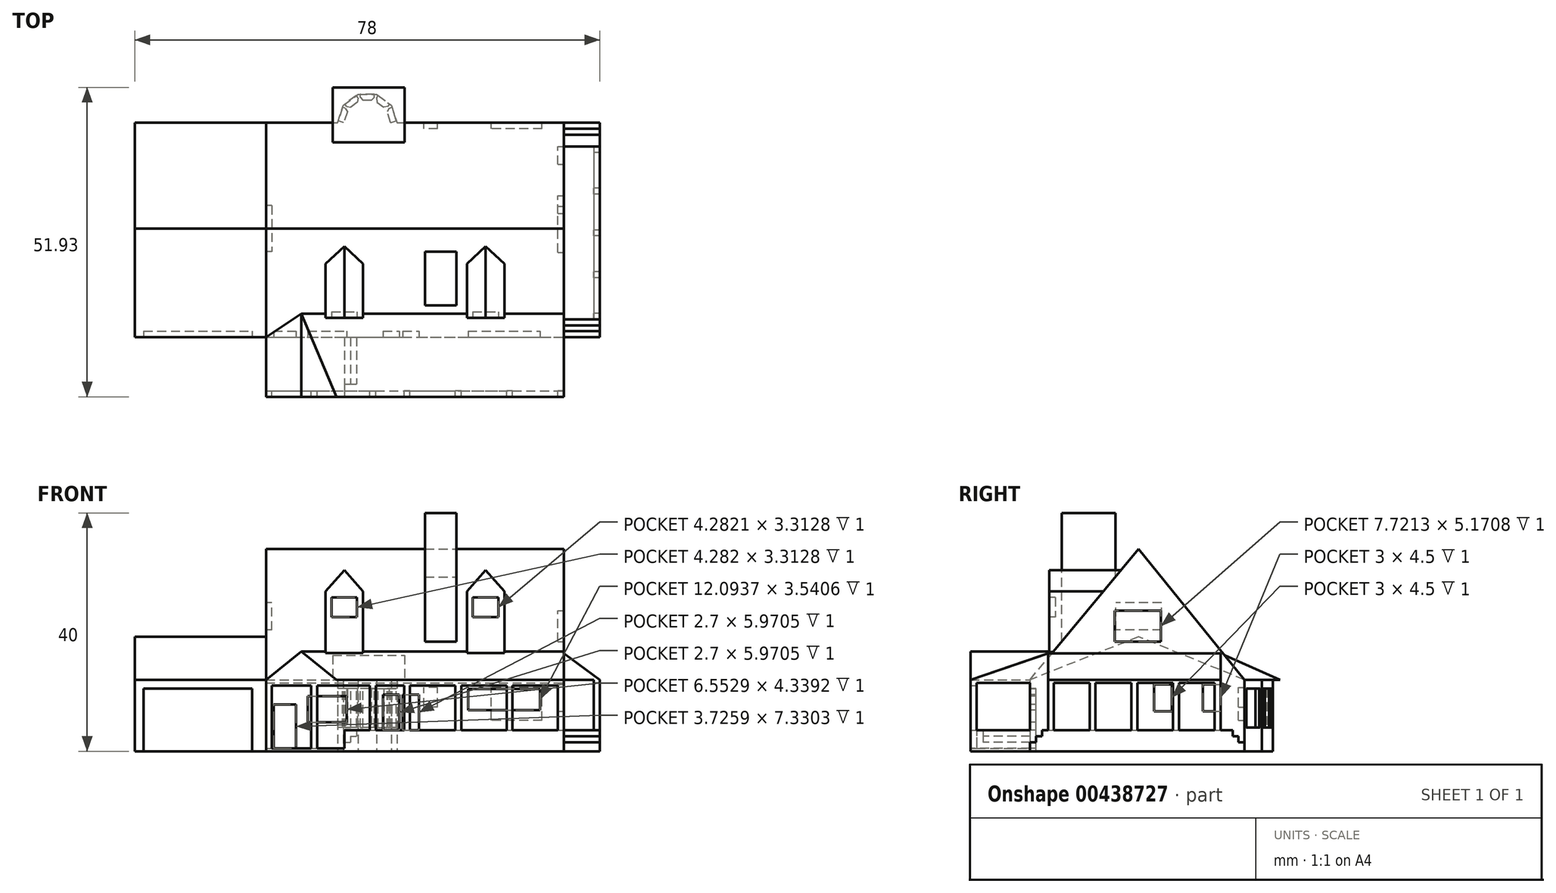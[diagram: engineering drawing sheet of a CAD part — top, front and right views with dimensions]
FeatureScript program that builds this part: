
annotation { "Feature Type Name" : "Feature", "Feature Type Description" : "" }
export const myFeature = defineFeature(function(context is Context, id is Id, definition is map)
    precondition{}
    {
        {
            var Q0;
            Q0=qCreatedBy(makeId("Top.planeOp"),FACE);
            var sketch = newSketch(context, id + "F0", { "sketchPlane" : qUnion([Q0])});
            skLineSegment(sketch, "E0.bottom", {"start": v(-54, 17.76) * mm, "end": v(18, 17.76) * mm});
            skLineSegment(sketch, "E0.top", {"start": v(-54, -18.24) * mm, "end": v(18, -18.24) * mm});
            skLineSegment(sketch, "E0.left", {"start": v(-54, 17.76) * mm, "end": v(-54, -18.24) * mm});
            skLineSegment(sketch, "E0.right", {"start": v(18, 17.76) * mm, "end": v(18, -18.24) * mm});
            skSolve(sketch);
        }
        {
            var Q0;
            Q0=makeQuery(id+"F0.imprint","IMPRINT",FACE,{"disambiguationData":[TD([[makeQuery(id+"F0.imprint","IMPRINT",EDGE,{"derivedFrom":sQuery(id+"F0.wireOp",EDGE,"E0.bottom")}),-1.0]])]});
            extrude(context, id + "F1", {"entities" : qUnion([Q0]), "depth" : 12 * mm});
        }
        {
            var Q0;
            Q0=makeQuery(id+"F1.opExtrude","SWEPT_FACE",FACE,{"disambiguationData":[OSD([sQuery(id+"F0.wireOp",EDGE,"E0.right")])]});
            var sketch = newSketch(context, id + "F2", { "sketchPlane" : qUnion([Q0])});
            skLineSegment(sketch, "E1.0", {"start": v(17.76, 12) * mm, "end": v(-18.24, 12) * mm});
            skLineSegment(sketch, "E2", {"start": v(-18.24, 12) * mm, "end": v(0, 33.97) * mm});
            skLineSegment(sketch, "E3", {"start": v(0, 33.97) * mm, "end": v(17.76, 12) * mm});
            skSolve(sketch);
        }
        {
            var Q0;
            Q0=makeQuery(id+"F2.imprint","IMPRINT",FACE,{"disambiguationData":[TD([[makeQuery(id+"F2.imprint","IMPRINT",EDGE,{"derivedFrom":sQuery(id+"F2.wireOp",EDGE,"E1.0")}),-1.0]])]});
            extrude(context, id + "F3", {"entities" : qUnion([Q0]), "operationType" : NewBodyOperationType.ADD, "oppositeDirection" : true, "depth" : 50 * mm});
        }
        {
            var Q0;
            Q0=makeQuery(id+"F1.opExtrude","SWEPT_FACE",FACE,{"disambiguationData":[OSD([sQuery(id+"F0.wireOp",EDGE,"E0.left")])]});
            var sketch = newSketch(context, id + "F4", { "sketchPlane" : qUnion([Q0])});
            skLineSegment(sketch, "E4.0", {"start": v(-17.76, 12) * mm, "end": v(18.24, 12) * mm});
            skLineSegment(sketch, "E5", {"start": v(-17.76, 12) * mm, "end": v(0, 19.2) * mm});
            skLineSegment(sketch, "E6", {"start": v(0, 19.2) * mm, "end": v(18.24, 12) * mm});
            skSolve(sketch);
        }
        {
            var Q0;
            Q0=makeQuery(id+"F4.imprint","IMPRINT",FACE,{"disambiguationData":[TD([[makeQuery(id+"F4.imprint","IMPRINT",EDGE,{"derivedFrom":sQuery(id+"F4.wireOp",EDGE,"E4.0")}),1.0]])]});
            extrude(context, id + "F5", {"entities" : qUnion([Q0]), "operationType" : NewBodyOperationType.ADD, "endBound" : BoundingType.UP_TO_NEXT, "oppositeDirection" : true, "depth" : 25 * mm});
        }
        {
            var Q0;
            Q0=makeQuery(id+"F1.opExtrude","SWEPT_FACE",FACE,{"disambiguationData":[OSD([sQuery(id+"F0.wireOp",EDGE,"E0.top")])]});
            var sketch = newSketch(context, id + "F6", { "sketchPlane" : qUnion([Q0])});
            skLineSegment(sketch, "E7.bottom", {"start": v(-32, 12) * mm, "end": v(18, 12) * mm});
            skLineSegment(sketch, "E7.top", {"start": v(-32, 11.5) * mm, "end": v(18, 11.5) * mm});
            skLineSegment(sketch, "E7.left", {"start": v(-32, 12) * mm, "end": v(-32, 11.5) * mm});
            skLineSegment(sketch, "E7.right", {"start": v(18, 12) * mm, "end": v(18, 11.5) * mm});
            skLineSegment(sketch, "E8", {"start": v(-32, 11.5) * mm, "end": v(-32, 0) * mm});
            skLineSegment(sketch, "E9.bottom", {"start": v(-32, 0) * mm, "end": v(18, 0) * mm});
            skLineSegment(sketch, "E9.top", {"start": v(-32, 0.5) * mm, "end": v(18, 0.5) * mm});
            skLineSegment(sketch, "E9.left", {"start": v(-32, 0) * mm, "end": v(-32, 0.5) * mm});
            skLineSegment(sketch, "E9.right", {"start": v(18, 0) * mm, "end": v(18, 0.5) * mm});
            skSolve(sketch);
        }
        {
            var Q0;
            Q0=makeQuery(id+"F6.imprint","IMPRINT",FACE,{"disambiguationData":[TD([[makeQuery(id+"F6.imprint","IMPRINT",EDGE,{"derivedFrom":sQuery(id+"F6.wireOp",EDGE,"E7.bottom")}),-1.0]])]});
            extrude(context, id + "F7", {"entities" : qUnion([Q0]), "operationType" : NewBodyOperationType.ADD, "depth" : 10 * mm});
        }
        {
            var Q0;
            Q0=makeQuery(id+"F6.imprint","IMPRINT",FACE,{"disambiguationData":[TD([[makeQuery(id+"F6.imprint","IMPRINT",EDGE,{"derivedFrom":sQuery(id+"F6.wireOp",EDGE,"E9.bottom")}),1.0]])]});
            extrude(context, id + "F8", {"entities" : qUnion([Q0]), "operationType" : NewBodyOperationType.ADD, "depth" : 10 * mm});
        }
        {
            var Q0;
            Q0=makeQuery(id+"F7.opExtrude","CAP_FACE",FACE,{"disambiguationData":[OSD([sQuery(id+"F6.wireOp",EDGE,"E7.bottom"),sQuery(id+"F6.wireOp",EDGE,"E7.top"),sQuery(id+"F6.wireOp",EDGE,"E7.left"),sQuery(id+"F6.wireOp",EDGE,"E7.right")])],"isStart":false});
            var sketch = newSketch(context, id + "F9", { "sketchPlane" : qUnion([Q0])});
            skLineSegment(sketch, "E10.0", {"start": v(-32, 12) * mm, "end": v(18, 12) * mm});
            skLineSegment(sketch, "E11", {"start": v(-32, 12) * mm, "end": v(-26.06, 16.73) * mm});
            skLineSegment(sketch, "E12", {"start": v(-26.06, 16.73) * mm, "end": v(-20.13, 12) * mm});
            skSolve(sketch);
        }
        {
            var Q0;
            {var subQ0=sQuery(id+"F9.wireOp",EDGE,"E11");Q0=makeQuery(id+"F9.imprint","IMPRINT",FACE,{"disambiguationData":[TD([[makeQuery(id+"F9.imprint","IMPRINT",EDGE,{"derivedFrom":subQ0}),-1.0]])]});}
            extrude(context, id + "F10", {"entities" : qUnion([Q0]), "operationType" : NewBodyOperationType.ADD, "endBound" : BoundingType.UP_TO_NEXT, "oppositeDirection" : true, "depth" : 25 * mm});
        }
        {
            var Q0;
            Q0=makeQuery(id+"F8.boolean.opBoolean","MERGE",FACE,{"derivedFrom":[makeQuery(id+"F7.boolean.opBoolean","MERGE",FACE,{"derivedFrom":[makeQuery(id+"F3.boolean.opBoolean","MERGE",FACE,{"derivedFrom":[makeQuery(id+"F1.opExtrude","SWEPT_FACE",FACE,{"disambiguationData":[OSD([sQuery(id+"F0.wireOp",EDGE,"E0.right")])]}),makeQuery(id+"F3.opExtrude","CAP_FACE",FACE,{"disambiguationData":[OSD([sQuery(id+"F2.wireOp",EDGE,"E1.0"),sQuery(id+"F2.wireOp",EDGE,"E2"),sQuery(id+"F2.wireOp",EDGE,"E3")])],"isStart":true})]}),makeQuery(id+"F7.opExtrude","SWEPT_FACE",FACE,{"disambiguationData":[OSD([sQuery(id+"F6.wireOp",EDGE,"E7.right")])]})]}),makeQuery(id+"F8.opExtrude","SWEPT_FACE",FACE,{"disambiguationData":[OSD([sQuery(id+"F6.wireOp",EDGE,"E9.right")])]})]});
            var sketch = newSketch(context, id + "F11", { "sketchPlane" : qUnion([Q0])});
            skLineSegment(sketch, "E13.0", {"start": v(-14.3, 16.73) * mm, "end": v(-28.24, 16.73) * mm});
            skLineSegment(sketch, "E14", {"start": v(-28.24, 12) * mm, "end": v(-14.3, 16.73) * mm});
            skSolve(sketch);
        }
        {
            var Q0;
            {var subQ0=sQuery(id+"F11.wireOp",EDGE,"E14");Q0=makeQuery(id+"F11.imprint","IMPRINT",FACE,{"disambiguationData":[TD([[makeQuery(id+"F11.imprint","IMPRINT",EDGE,{"derivedFrom":subQ0}),-1.0]])]});}
            extrude(context, id + "F12", {"entities" : qUnion([Q0]), "operationType" : NewBodyOperationType.ADD, "endBound" : BoundingType.UP_TO_NEXT, "oppositeDirection" : true, "depth" : 25 * mm});
        }
        {
            var Q0;
            Q0=makeQuery(id+"F8.opExtrude","SWEPT_FACE",FACE,{"disambiguationData":[OSD([sQuery(id+"F6.wireOp",EDGE,"E9.top")])]});
            var sketch = newSketch(context, id + "F13", { "sketchPlane" : qUnion([Q0])});
            skLineSegment(sketch, "E15", {"start": v(-18.82, -18.24) * mm, "end": v(-18.82, -28.24) * mm});
            skLineSegment(sketch, "E16", {"start": v(-17.82, -18.24) * mm, "end": v(-17.82, -28.24) * mm});
            skLineSegment(sketch, "E17", {"start": v(-16.82, -18.24) * mm, "end": v(-16.82, -28.24) * mm});
            skLineSegment(sketch, "E18.bottom", {"start": v(-32, -28.24) * mm, "end": v(-31, -28.24) * mm});
            skLineSegment(sketch, "E18.top", {"start": v(-32, -27.24) * mm, "end": v(-31, -27.24) * mm});
            skLineSegment(sketch, "E18.left", {"start": v(-32, -28.24) * mm, "end": v(-32, -27.24) * mm});
            skLineSegment(sketch, "E18.right", {"start": v(-31, -28.24) * mm, "end": v(-31, -27.24) * mm});
            skLineSegment(sketch, "E19.bottom", {"start": v(-24.4, -28.24) * mm, "end": v(-23.4, -28.24) * mm});
            skLineSegment(sketch, "E19.top", {"start": v(-24.4, -27.24) * mm, "end": v(-23.4, -27.24) * mm});
            skLineSegment(sketch, "E19.left", {"start": v(-24.4, -28.24) * mm, "end": v(-24.4, -27.24) * mm});
            skLineSegment(sketch, "E19.right", {"start": v(-23.4, -28.24) * mm, "end": v(-23.4, -27.24) * mm});
            skLineSegment(sketch, "E20", {"start": v(-31, -27.74) * mm, "end": v(-24.4, -27.74) * mm, "construction": true});
            skLineSegment(sketch, "E21", {"start": v(-23.4, -27.74) * mm, "end": v(-16.82, -27.51) * mm, "construction": true});
            skSolve(sketch);
        }
        {
            var Q0;
            {var subQ0=sQuery(id+"F13.wireOp",EDGE,"E15");Q0=makeQuery(id+"F13.imprint","IMPRINT",FACE,{"disambiguationData":[TD([[makeQuery(id+"F13.imprint","IMPRINT",EDGE,{"derivedFrom":subQ0}),1.0]])]});}
            extrude(context, id + "F14", {"entities" : qUnion([Q0]), "operationType" : NewBodyOperationType.ADD, "depth" : 1 * mm});
        }
        {
            var Q0;
            {var subQ0=sQuery(id+"F13.wireOp",EDGE,"E16");Q0=makeQuery(id+"F13.imprint","IMPRINT",FACE,{"disambiguationData":[TD([[makeQuery(id+"F13.imprint","IMPRINT",EDGE,{"derivedFrom":subQ0}),1.0]])]});}
            extrude(context, id + "F15", {"entities" : qUnion([Q0]), "operationType" : NewBodyOperationType.ADD, "depth" : 2 * mm});
        }
        {
            var Q0;
            {var subQ0=sQuery(id+"F13.wireOp",EDGE,"E17");Q0=makeQuery(id+"F13.imprint","IMPRINT",FACE,{"disambiguationData":[TD([[makeQuery(id+"F13.imprint","IMPRINT",EDGE,{"derivedFrom":subQ0}),1.0]])]});}
            extrude(context, id + "F16", {"entities" : qUnion([Q0]), "operationType" : NewBodyOperationType.ADD, "depth" : 3 * mm});
        }
        {
            var Q0;
            Q0=makeQuery(id+"F16.opExtrude","CAP_FACE",FACE,{"disambiguationData":[OSD([sQuery(id+"F0.wireOp",EDGE,"E0.top"),sQuery(id+"F0.wireOp",EDGE,"E0.right"),sQuery(id+"F6.wireOp",EDGE,"E9.top"),sQuery(id+"F6.wireOp",EDGE,"E9.right"),sQuery(id+"F13.wireOp",EDGE,"E17")])],"isStart":false});
            var sketch = newSketch(context, id + "F17", { "sketchPlane" : qUnion([Q0])});
            skLineSegment(sketch, "E22.bottom", {"start": v(18, -28.24) * mm, "end": v(17, -28.24) * mm});
            skLineSegment(sketch, "E22.top", {"start": v(18, -27.24) * mm, "end": v(17, -27.24) * mm});
            skLineSegment(sketch, "E22.left", {"start": v(18, -28.24) * mm, "end": v(18, -27.24) * mm});
            skLineSegment(sketch, "E22.right", {"start": v(17, -28.24) * mm, "end": v(17, -27.24) * mm});
            skLineSegment(sketch, "E23.bottom", {"start": v(9.4, -28.24) * mm, "end": v(8.4, -28.24) * mm});
            skLineSegment(sketch, "E23.top", {"start": v(9.4, -27.24) * mm, "end": v(8.4, -27.24) * mm});
            skLineSegment(sketch, "E23.left", {"start": v(9.4, -28.24) * mm, "end": v(9.4, -27.24) * mm});
            skLineSegment(sketch, "E23.right", {"start": v(8.4, -28.24) * mm, "end": v(8.4, -27.24) * mm});
            skLineSegment(sketch, "E24.bottom", {"start": v(0.79, -28.24) * mm, "end": v(-0.21, -28.24) * mm});
            skLineSegment(sketch, "E24.top", {"start": v(0.79, -27.24) * mm, "end": v(-0.21, -27.24) * mm});
            skLineSegment(sketch, "E24.left", {"start": v(0.79, -28.24) * mm, "end": v(0.79, -27.24) * mm});
            skLineSegment(sketch, "E24.right", {"start": v(-0.21, -28.24) * mm, "end": v(-0.21, -27.24) * mm});
            skLineSegment(sketch, "E25.bottom", {"start": v(-7.82, -28.24) * mm, "end": v(-8.82, -28.24) * mm});
            skLineSegment(sketch, "E25.top", {"start": v(-7.82, -27.24) * mm, "end": v(-8.82, -27.24) * mm});
            skLineSegment(sketch, "E25.left", {"start": v(-7.82, -28.24) * mm, "end": v(-7.82, -27.24) * mm});
            skLineSegment(sketch, "E25.right", {"start": v(-8.82, -28.24) * mm, "end": v(-8.82, -27.24) * mm});
            skLineSegment(sketch, "E26", {"start": v(-7.82, -27.74) * mm, "end": v(-0.21, -27.74) * mm, "construction": true});
            skLineSegment(sketch, "E27", {"start": v(0.79, -27.74) * mm, "end": v(8.4, -27.74) * mm, "construction": true});
            skLineSegment(sketch, "E28", {"start": v(9.4, -27.74) * mm, "end": v(17, -27.74) * mm, "construction": true});
            skLineSegment(sketch, "E29.bottom", {"start": v(-14.58, -28.24) * mm, "end": v(-13.58, -28.24) * mm});
            skLineSegment(sketch, "E29.top", {"start": v(-14.58, -27.24) * mm, "end": v(-13.58, -27.24) * mm});
            skLineSegment(sketch, "E29.left", {"start": v(-14.58, -28.24) * mm, "end": v(-14.58, -27.24) * mm});
            skLineSegment(sketch, "E29.right", {"start": v(-13.58, -28.24) * mm, "end": v(-13.58, -27.24) * mm});
            skSolve(sketch);
        }
        {
            var Q0;
            Q0=makeQuery(id+"F17.imprint","IMPRINT",FACE,{"disambiguationData":[TD([[makeQuery(id+"F17.imprint","IMPRINT",EDGE,{"derivedFrom":sQuery(id+"F17.wireOp",EDGE,"E29.bottom")}),1.0]])]});
            extrude(context, id + "F18", {"entities" : qUnion([Q0]), "operationType" : NewBodyOperationType.ADD, "endBound" : BoundingType.UP_TO_NEXT, "depth" : 25 * mm});
        }
        {
            var Q0;
            Q0=makeQuery(id+"F17.imprint","IMPRINT",FACE,{"disambiguationData":[TD([[makeQuery(id+"F17.imprint","IMPRINT",EDGE,{"derivedFrom":sQuery(id+"F17.wireOp",EDGE,"E25.bottom")}),1.0]])]});
            extrude(context, id + "F19", {"entities" : qUnion([Q0]), "operationType" : NewBodyOperationType.ADD, "endBound" : BoundingType.UP_TO_NEXT, "depth" : 25 * mm});
        }
        {
            var Q0;
            Q0=makeQuery(id+"F17.imprint","IMPRINT",FACE,{"disambiguationData":[TD([[makeQuery(id+"F17.imprint","IMPRINT",EDGE,{"derivedFrom":sQuery(id+"F17.wireOp",EDGE,"E24.bottom")}),1.0]])]});
            extrude(context, id + "F20", {"entities" : qUnion([Q0]), "operationType" : NewBodyOperationType.ADD, "endBound" : BoundingType.UP_TO_NEXT, "depth" : 25 * mm});
        }
        {
            var Q0;
            Q0=makeQuery(id+"F17.imprint","IMPRINT",FACE,{"disambiguationData":[TD([[makeQuery(id+"F17.imprint","IMPRINT",EDGE,{"derivedFrom":sQuery(id+"F17.wireOp",EDGE,"E23.bottom")}),1.0]])]});
            extrude(context, id + "F21", {"entities" : qUnion([Q0]), "operationType" : NewBodyOperationType.ADD, "endBound" : BoundingType.UP_TO_NEXT, "depth" : 25 * mm});
        }
        {
            var Q0;
            Q0=makeQuery(id+"F17.imprint","IMPRINT",FACE,{"disambiguationData":[TD([[makeQuery(id+"F17.imprint","IMPRINT",EDGE,{"derivedFrom":sQuery(id+"F17.wireOp",EDGE,"E22.bottom")}),1.0]])]});
            extrude(context, id + "F22", {"entities" : qUnion([Q0]), "operationType" : NewBodyOperationType.ADD, "endBound" : BoundingType.UP_TO_NEXT, "depth" : 25 * mm});
        }
        {
            var Q0;
            Q0=makeQuery(id+"F13.imprint","IMPRINT",FACE,{"disambiguationData":[TD([[makeQuery(id+"F13.imprint","IMPRINT",EDGE,{"derivedFrom":sQuery(id+"F13.wireOp",EDGE,"E18.bottom")}),1.0]])]});
            extrude(context, id + "F23", {"entities" : qUnion([Q0]), "operationType" : NewBodyOperationType.ADD, "endBound" : BoundingType.UP_TO_NEXT, "depth" : 25 * mm});
        }
        {
            var Q0;
            Q0=makeQuery(id+"F13.imprint","IMPRINT",FACE,{"disambiguationData":[TD([[makeQuery(id+"F13.imprint","IMPRINT",EDGE,{"derivedFrom":sQuery(id+"F13.wireOp",EDGE,"E19.bottom")}),1.0]])]});
            extrude(context, id + "F24", {"entities" : qUnion([Q0]), "operationType" : NewBodyOperationType.ADD, "endBound" : BoundingType.UP_TO_NEXT, "depth" : 25 * mm});
        }
        {
            var Q0;
            Q0=makeQuery(id+"F14.opExtrude","CAP_FACE",FACE,{"disambiguationData":[OSD([sQuery(id+"F6.wireOp",EDGE,"E9.top"),sQuery(id+"F13.wireOp",EDGE,"E15"),sQuery(id+"F13.wireOp",EDGE,"E16")])],"isStart":false});
            var sketch = newSketch(context, id + "F25", { "sketchPlane" : qUnion([Q0])});
            skLineSegment(sketch, "E30", {"start": v(-18.82, -26.1) * mm, "end": v(-17.82, -26.1) * mm});
            skSolve(sketch);
        }
        {
            var Q0;
            Q0=makeQuery(id+"F15.opExtrude","CAP_FACE",FACE,{"disambiguationData":[OSD([sQuery(id+"F6.wireOp",EDGE,"E9.top"),sQuery(id+"F13.wireOp",EDGE,"E16"),sQuery(id+"F13.wireOp",EDGE,"E17")])],"isStart":false});
            var sketch = newSketch(context, id + "F26", { "sketchPlane" : qUnion([Q0])});
            skPoint(sketch, "E31.0", {"position": v(-17.82, -26.1) * mm});
            skLineSegment(sketch, "E32", {"start": v(-17.82, -26.1) * mm, "end": v(-16.82, -26.1) * mm});
            skSolve(sketch);
        }
        {
            var Q0;
            {var subQ0=sQuery(id+"F25.wireOp",EDGE,"E30");Q0=makeQuery(id+"F25.imprint","IMPRINT",FACE,{"disambiguationData":[TD([[makeQuery(id+"F25.imprint","IMPRINT",EDGE,{"derivedFrom":subQ0}),-1.0]])]});}
            extrude(context, id + "F27", {"entities" : qUnion([Q0]), "operationType" : NewBodyOperationType.ADD, "depth" : 2 * mm});
        }
        {
            var Q0;
            {var subQ0=sQuery(id+"F26.wireOp",EDGE,"E32");Q0=makeQuery(id+"F26.imprint","IMPRINT",FACE,{"disambiguationData":[TD([[makeQuery(id+"F26.imprint","IMPRINT",EDGE,{"derivedFrom":subQ0}),-1.0]])]});}
            extrude(context, id + "F28", {"entities" : qUnion([Q0]), "operationType" : NewBodyOperationType.ADD, "depth" : 1 * mm});
        }
        {
            var Q0;
            {var subQ0=sQuery(id+"F6.wireOp",EDGE,"E9.right");var subQ1=sQuery(id+"F0.wireOp",EDGE,"E0.right");var subQ2=sQuery(id+"F6.wireOp",EDGE,"E7.right");var subQ3=sQuery(id+"F2.wireOp",EDGE,"E2");Q0=makeQuery(id+"F22.boolean.opBoolean","MERGE",FACE,{"derivedFrom":[makeQuery(id+"F16.boolean.opBoolean","MERGE",FACE,{"derivedFrom":[makeQuery(id+"F12.boolean.opBoolean","MERGE",FACE,{"derivedFrom":[makeQuery(id+"F8.boolean.opBoolean","MERGE",FACE,{"derivedFrom":[makeQuery(id+"F7.boolean.opBoolean","MERGE",FACE,{"derivedFrom":[makeQuery(id+"F3.boolean.opBoolean","MERGE",FACE,{"derivedFrom":[makeQuery(id+"F1.opExtrude","SWEPT_FACE",FACE,{"disambiguationData":[OSD([subQ1])]}),makeQuery(id+"F3.opExtrude","CAP_FACE",FACE,{"disambiguationData":[OSD([sQuery(id+"F2.wireOp",EDGE,"E1.0"),subQ3,sQuery(id+"F2.wireOp",EDGE,"E3")])],"isStart":true})]}),makeQuery(id+"F7.opExtrude","SWEPT_FACE",FACE,{"disambiguationData":[OSD([subQ2])]})]}),makeQuery(id+"F8.opExtrude","SWEPT_FACE",FACE,{"disambiguationData":[OSD([subQ0])]})]}),makeQuery(id+"F12.opExtrude","CAP_FACE",FACE,{"disambiguationData":[OSD([subQ3,sQuery(id+"F6.wireOp",EDGE,"E7.bottom"),subQ2,sQuery(id+"F11.wireOp",EDGE,"E14")])],"isStart":true})]}),makeQuery(id+"F16.opExtrude","SWEPT_FACE",FACE,{"disambiguationData":[OSD([sQuery(id+"F0.wireOp",EDGE,"E0.top"),subQ1,sQuery(id+"F6.wireOp",EDGE,"E9.top"),subQ0])]})]}),makeQuery(id+"F22.opExtrude","SWEPT_FACE",FACE,{"disambiguationData":[OSD([sQuery(id+"F17.wireOp",EDGE,"E22.left")])]})]});}
            var sketch = newSketch(context, id + "F29", { "sketchPlane" : qUnion([Q0])});
            skLineSegment(sketch, "E33.0", {"start": v(-18.24, 11.5) * mm, "end": v(-18.24, 3.5) * mm});
            skLineSegment(sketch, "E34", {"start": v(-18.24, 3.5) * mm, "end": v(-18.24, 0) * mm});
            skLineSegment(sketch, "E35", {"start": v(-18.24, 3.5) * mm, "end": v(17.76, 3.5) * mm});
            skLineSegment(sketch, "E36", {"start": v(-14.3, 16.73) * mm, "end": v(13.94, 16.73) * mm, "construction": true});
            skLineSegment(sketch, "E37.bottom", {"start": v(-4, 18.4) * mm, "end": v(3.72, 18.4) * mm});
            skLineSegment(sketch, "E37.top", {"start": v(-4, 23.58) * mm, "end": v(3.72, 23.58) * mm});
            skLineSegment(sketch, "E37.left", {"start": v(-4, 18.4) * mm, "end": v(-4, 23.58) * mm});
            skLineSegment(sketch, "E37.right", {"start": v(3.72, 18.4) * mm, "end": v(3.72, 23.58) * mm});
            skLineSegment(sketch, "E38", {"start": v(-4, 21) * mm, "end": v(-10.77, 21) * mm, "construction": true});
            skLineSegment(sketch, "E39", {"start": v(3.72, 21) * mm, "end": v(10.5, 21) * mm, "construction": true});
            skLineSegment(sketch, "E40", {"start": v(0, 33.97) * mm, "end": v(0, 23.58) * mm, "construction": true});
            skLineSegment(sketch, "E41.bottom", {"start": v(-12.85, 3.5) * mm, "end": v(-9.57, 3.5) * mm});
            skLineSegment(sketch, "E41.top", {"start": v(-12.85, 10.16) * mm, "end": v(-9.57, 10.16) * mm});
            skLineSegment(sketch, "E41.left", {"start": v(-12.85, 3.5) * mm, "end": v(-12.85, 10.16) * mm});
            skLineSegment(sketch, "E41.right", {"start": v(-9.57, 3.5) * mm, "end": v(-9.57, 10.16) * mm});
            skLineSegment(sketch, "E42.bottom", {"start": v(-8.97, 3.5) * mm, "end": v(-5.69, 3.5) * mm});
            skLineSegment(sketch, "E42.top", {"start": v(-8.97, 10.16) * mm, "end": v(-5.69, 10.16) * mm});
            skLineSegment(sketch, "E42.left", {"start": v(-8.97, 3.5) * mm, "end": v(-8.97, 10.16) * mm});
            skLineSegment(sketch, "E42.right", {"start": v(-5.69, 3.5) * mm, "end": v(-5.69, 10.16) * mm});
            skLineSegment(sketch, "E43.bottom", {"start": v(2.54, 6.72) * mm, "end": v(5.54, 6.72) * mm});
            skLineSegment(sketch, "E43.top", {"start": v(2.54, 11.22) * mm, "end": v(5.54, 11.22) * mm});
            skLineSegment(sketch, "E43.left", {"start": v(2.54, 6.72) * mm, "end": v(2.54, 11.22) * mm});
            skLineSegment(sketch, "E43.right", {"start": v(5.54, 6.72) * mm, "end": v(5.54, 11.22) * mm});
            skLineSegment(sketch, "E44.bottom", {"start": v(10.77, 11.22) * mm, "end": v(13.77, 11.22) * mm});
            skLineSegment(sketch, "E44.top", {"start": v(10.77, 6.72) * mm, "end": v(13.77, 6.72) * mm});
            skLineSegment(sketch, "E44.left", {"start": v(10.77, 11.22) * mm, "end": v(10.77, 6.72) * mm});
            skLineSegment(sketch, "E44.right", {"start": v(13.77, 11.22) * mm, "end": v(13.77, 6.72) * mm});
            skSolve(sketch);
        }
        {
            var Q0;
            {var subQ0=sQuery(id+"F29.wireOp",EDGE,"E34");Q0=makeQuery(id+"F29.imprint","IMPRINT",FACE,{"disambiguationData":[TD([[makeQuery(id+"F29.imprint","IMPRINT",EDGE,{"derivedFrom":subQ0}),1.0]])]});}
            extrude(context, id + "F30", {"entities" : qUnion([Q0]), "operationType" : NewBodyOperationType.ADD, "depth" : 6 * mm});
        }
        {
            var Q0;
            Q0=makeQuery(id+"F30.opExtrude","SWEPT_FACE",FACE,{"disambiguationData":[OSD([sQuery(id+"F29.wireOp",EDGE,"E35")])]});
            var sketch = newSketch(context, id + "F31", { "sketchPlane" : qUnion([Q0])});
            skLineSegment(sketch, "E45", {"start": v(18, -17.24) * mm, "end": v(24, -17.24) * mm});
            skLineSegment(sketch, "E46", {"start": v(18, -16.24) * mm, "end": v(24, -16.24) * mm});
            skLineSegment(sketch, "E47", {"start": v(24, 16.76) * mm, "end": v(18, 16.76) * mm});
            skLineSegment(sketch, "E48", {"start": v(24, 15.76) * mm, "end": v(18, 15.76) * mm});
            skSolve(sketch);
        }
        {
            var Q0;
            {var subQ0=sQuery(id+"F31.wireOp",EDGE,"E45");Q0=makeQuery(id+"F31.imprint","IMPRINT",FACE,{"disambiguationData":[TD([[makeQuery(id+"F31.imprint","IMPRINT",EDGE,{"derivedFrom":subQ0}),-1.0]])]});}
            extrude(context, id + "F32", {"entities" : qUnion([Q0]), "operationType" : NewBodyOperationType.REMOVE, "oppositeDirection" : true, "depth" : 2 * mm});
        }
        {
            var Q0;
            {var subQ0=sQuery(id+"F31.wireOp",EDGE,"E45");Q0=makeQuery(id+"F31.imprint","IMPRINT",FACE,{"disambiguationData":[TD([[makeQuery(id+"F31.imprint","IMPRINT",EDGE,{"derivedFrom":subQ0}),1.0]])]});}
            extrude(context, id + "F33", {"entities" : qUnion([Q0]), "operationType" : NewBodyOperationType.REMOVE, "oppositeDirection" : true, "depth" : 1 * mm});
        }
        {
            var Q0;
            {var subQ0=sQuery(id+"F31.wireOp",EDGE,"E47");Q0=makeQuery(id+"F31.imprint","IMPRINT",FACE,{"disambiguationData":[TD([[makeQuery(id+"F31.imprint","IMPRINT",EDGE,{"derivedFrom":subQ0}),-1.0]])]});}
            extrude(context, id + "F34", {"entities" : qUnion([Q0]), "operationType" : NewBodyOperationType.REMOVE, "oppositeDirection" : true, "depth" : 2 * mm});
        }
        {
            var Q0;
            {var subQ0=sQuery(id+"F31.wireOp",EDGE,"E47");Q0=makeQuery(id+"F31.imprint","IMPRINT",FACE,{"disambiguationData":[TD([[makeQuery(id+"F31.imprint","IMPRINT",EDGE,{"derivedFrom":subQ0}),1.0]])]});}
            extrude(context, id + "F35", {"entities" : qUnion([Q0]), "operationType" : NewBodyOperationType.REMOVE, "oppositeDirection" : true, "depth" : 1 * mm});
        }
        {
            var Q0;
            {var subQ0=sQuery(id+"F0.wireOp",EDGE,"E0.bottom");Q0=makeQuery(id+"F30.boolean.opBoolean","MERGE",FACE,{"derivedFrom":[makeQuery(id+"F1.opExtrude","SWEPT_FACE",FACE,{"disambiguationData":[OSD([subQ0])]}),makeQuery(id+"F30.opExtrude","SWEPT_FACE",FACE,{"disambiguationData":[OSD([subQ0,sQuery(id+"F0.wireOp",EDGE,"E0.right")])]})]});}
            var sketch = newSketch(context, id + "F36", { "sketchPlane" : qUnion([Q0])});
            skLineSegment(sketch, "E49.0", {"start": v(-18, 33.97) * mm, "end": v(-18, 12) * mm});
            skPoint(sketch, "E50.0", {"position": v(-24, 3.5) * mm});
            skLineSegment(sketch, "E51", {"start": v(-24, 3.5) * mm, "end": v(-24, 12) * mm, "construction": true});
            skLineSegment(sketch, "E52", {"start": v(-24, 12) * mm, "end": v(-18, 12) * mm});
            skLineSegment(sketch, "E53", {"start": v(-24, 12) * mm, "end": v(-18, 16.4) * mm});
            skSolve(sketch);
        }
        {
            var Q0;
            {var subQ0=sQuery(id+"F36.wireOp",EDGE,"E52");Q0=makeQuery(id+"F36.imprint","IMPRINT",FACE,{"disambiguationData":[TD([[makeQuery(id+"F36.imprint","IMPRINT",EDGE,{"derivedFrom":subQ0}),1.0]])]});}
            extrude(context, id + "F37", {"entities" : qUnion([Q0]), "operationType" : NewBodyOperationType.ADD, "oppositeDirection" : true, "depth" : 33 * mm, "hasSecondDirection" : true, "secondDirectionOppositeDirection" : true, "secondDirectionDepth" : 4 * mm});
        }
        {
            var Q0;
            {var subQ0=sQuery(id+"F31.wireOp",EDGE,"E46");Q0=makeQuery(id+"F31.imprint","IMPRINT",FACE,{"disambiguationData":[TD([[makeQuery(id+"F31.imprint","IMPRINT",EDGE,{"derivedFrom":subQ0}),1.0]])]});}
            var sketch = newSketch(context, id + "F38", { "sketchPlane" : qUnion([Q0])});
            skPoint(sketch, "E54.0", {"position": v(24, -15.24) * mm});
            skPoint(sketch, "E55.0", {"position": v(24, 13.76) * mm});
            skLineSegment(sketch, "E56.bottom", {"start": v(24, -15.24) * mm, "end": v(23, -15.24) * mm});
            skLineSegment(sketch, "E56.top", {"start": v(24, -14.24) * mm, "end": v(23, -14.24) * mm});
            skLineSegment(sketch, "E56.left", {"start": v(24, -15.24) * mm, "end": v(24, -14.24) * mm});
            skLineSegment(sketch, "E56.right", {"start": v(23, -15.24) * mm, "end": v(23, -14.24) * mm});
            skLineSegment(sketch, "E57.0", {"start": v(24, -16.24) * mm, "end": v(24, 15.76) * mm});
            skLineSegment(sketch, "E58.bottom", {"start": v(24, -8.24) * mm, "end": v(23, -8.24) * mm});
            skLineSegment(sketch, "E58.top", {"start": v(24, -7.24) * mm, "end": v(23, -7.24) * mm});
            skLineSegment(sketch, "E58.left", {"start": v(24, -8.24) * mm, "end": v(24, -7.24) * mm});
            skLineSegment(sketch, "E58.right", {"start": v(23, -8.24) * mm, "end": v(23, -7.24) * mm});
            skLineSegment(sketch, "E59.bottom", {"start": v(24, -1.24) * mm, "end": v(23, -1.24) * mm});
            skLineSegment(sketch, "E59.top", {"start": v(24, -0.24) * mm, "end": v(23, -0.24) * mm});
            skLineSegment(sketch, "E59.left", {"start": v(24, -1.24) * mm, "end": v(24, -0.24) * mm});
            skLineSegment(sketch, "E59.right", {"start": v(23, -1.24) * mm, "end": v(23, -0.24) * mm});
            skLineSegment(sketch, "E60.bottom", {"start": v(24, 5.76) * mm, "end": v(23, 5.76) * mm});
            skLineSegment(sketch, "E60.top", {"start": v(24, 6.76) * mm, "end": v(23, 6.76) * mm});
            skLineSegment(sketch, "E60.left", {"start": v(24, 5.76) * mm, "end": v(24, 6.76) * mm});
            skLineSegment(sketch, "E60.right", {"start": v(23, 5.76) * mm, "end": v(23, 6.76) * mm});
            skLineSegment(sketch, "E61.bottom", {"start": v(24, 13.76) * mm, "end": v(23, 13.76) * mm});
            skLineSegment(sketch, "E61.top", {"start": v(24, 12.76) * mm, "end": v(23, 12.76) * mm});
            skLineSegment(sketch, "E61.left", {"start": v(24, 13.76) * mm, "end": v(24, 12.76) * mm});
            skLineSegment(sketch, "E61.right", {"start": v(23, 13.76) * mm, "end": v(23, 12.76) * mm});
            skLineSegment(sketch, "E62", {"start": v(23.5, 12.76) * mm, "end": v(23.5, 6.76) * mm, "construction": true});
            skLineSegment(sketch, "E63", {"start": v(23.5, 5.76) * mm, "end": v(23.5, -0.24) * mm, "construction": true});
            skLineSegment(sketch, "E64", {"start": v(23.5, -1.24) * mm, "end": v(23.5, -7.24) * mm, "construction": true});
            skLineSegment(sketch, "E65", {"start": v(23.5, -8.24) * mm, "end": v(23.5, -14.24) * mm, "construction": true});
            skSolve(sketch);
        }
        {
            var Q0;
            {var subQ0=sQuery(id+"F38.wireOp",EDGE,"E56.bottom");Q0=makeQuery(id+"F38.imprint","IMPRINT",FACE,{"disambiguationData":[TD([[makeQuery(id+"F38.imprint","IMPRINT",EDGE,{"derivedFrom":subQ0}),-1.0]])]});}
            extrude(context, id + "F39", {"entities" : qUnion([Q0]), "operationType" : NewBodyOperationType.ADD, "endBound" : BoundingType.UP_TO_NEXT, "depth" : 25 * mm});
        }
        {
            var Q0;
            Q0=makeQuery(id+"F38.imprint","IMPRINT",FACE,{"disambiguationData":[TD([[makeQuery(id+"F38.imprint","IMPRINT",EDGE,{"derivedFrom":sQuery(id+"F38.wireOp",EDGE,"E58.bottom")}),-1.0]])]});
            extrude(context, id + "F40", {"entities" : qUnion([Q0]), "operationType" : NewBodyOperationType.ADD, "endBound" : BoundingType.UP_TO_NEXT, "depth" : 25 * mm});
        }
        {
            var Q0;
            Q0=makeQuery(id+"F38.imprint","IMPRINT",FACE,{"disambiguationData":[TD([[makeQuery(id+"F38.imprint","IMPRINT",EDGE,{"derivedFrom":sQuery(id+"F38.wireOp",EDGE,"E59.bottom")}),-1.0]])]});
            extrude(context, id + "F41", {"entities" : qUnion([Q0]), "operationType" : NewBodyOperationType.ADD, "endBound" : BoundingType.UP_TO_NEXT, "depth" : 25 * mm});
        }
        {
            var Q0;
            Q0=makeQuery(id+"F38.imprint","IMPRINT",FACE,{"disambiguationData":[TD([[makeQuery(id+"F38.imprint","IMPRINT",EDGE,{"derivedFrom":sQuery(id+"F38.wireOp",EDGE,"E60.bottom")}),-1.0]])]});
            extrude(context, id + "F42", {"entities" : qUnion([Q0]), "operationType" : NewBodyOperationType.ADD, "endBound" : BoundingType.UP_TO_NEXT, "depth" : 25 * mm});
        }
        {
            var Q0;
            Q0=makeQuery(id+"F38.imprint","IMPRINT",FACE,{"disambiguationData":[TD([[makeQuery(id+"F38.imprint","IMPRINT",EDGE,{"derivedFrom":sQuery(id+"F38.wireOp",EDGE,"E61.bottom")}),1.0]])]});
            extrude(context, id + "F43", {"entities" : qUnion([Q0]), "operationType" : NewBodyOperationType.ADD, "endBound" : BoundingType.UP_TO_NEXT, "depth" : 25 * mm});
        }
        {
            var Q0;
            Q0=qCreatedBy(makeId("Front.planeOp"),FACE);
            cPlane(context, id + "F44", {"entities" : qUnion([Q0]), "cplaneType" : CPlaneType.OFFSET, "offset" : 15 * mm, "width" : 150 * mm, "height" : 150 * mm});
        }
        {
            var Q0;
            Q0=qCreatedBy(id+"F44.planeOp",FACE);
            var sketch = newSketch(context, id + "F45", { "sketchPlane" : qUnion([Q0])});
            skLineSegment(sketch, "E66.bottom", {"start": v(-22, 21.09) * mm, "end": v(-15.7, 21.09) * mm});
            skLineSegment(sketch, "E66.top", {"start": v(-22, 26.81) * mm, "end": v(-15.7, 26.81) * mm});
            skLineSegment(sketch, "E66.left", {"start": v(-22, 21.09) * mm, "end": v(-22, 26.81) * mm});
            skLineSegment(sketch, "E66.right", {"start": v(-15.7, 21.09) * mm, "end": v(-15.7, 26.81) * mm});
            skLineSegment(sketch, "E67", {"start": v(-22, 26.81) * mm, "end": v(-18.85, 30.4) * mm});
            skPoint(sketch, "E67.endSnap0", {"position": v(-18.85, 26.81) * mm});
            skLineSegment(sketch, "E68", {"start": v(-18.85, 30.4) * mm, "end": v(-15.7, 26.81) * mm});
            skLineSegment(sketch, "E69.0", {"start": v(-32, 12) * mm, "end": v(-32, 33.97) * mm});
            skLineSegment(sketch, "E70.0", {"start": v(18, 16.73) * mm, "end": v(18, 33.97) * mm});
            skLineSegment(sketch, "E71", {"start": v(-22, 23.95) * mm, "end": v(-32, 23.95) * mm, "construction": true});
            skLineSegment(sketch, "E72.bottom", {"start": v(1.73, 21.09) * mm, "end": v(8, 21.09) * mm});
            skLineSegment(sketch, "E72.top", {"start": v(1.73, 26.81) * mm, "end": v(8, 26.81) * mm});
            skLineSegment(sketch, "E72.left", {"start": v(1.73, 21.09) * mm, "end": v(1.73, 26.81) * mm});
            skLineSegment(sketch, "E72.right", {"start": v(8, 21.09) * mm, "end": v(8, 26.81) * mm});
            skLineSegment(sketch, "E73", {"start": v(1.73, 26.81) * mm, "end": v(4.87, 30.4) * mm});
            skPoint(sketch, "E73.endSnap0", {"position": v(4.87, 26.81) * mm});
            skLineSegment(sketch, "E74", {"start": v(4.87, 30.4) * mm, "end": v(8, 26.81) * mm});
            skLineSegment(sketch, "E75", {"start": v(8, 23.95) * mm, "end": v(18, 23.95) * mm, "construction": true});
            skSolve(sketch);
        }
        {
            var Q0;
            Q0=makeQuery(id+"F45.imprint","IMPRINT",FACE,{"disambiguationData":[TD([[makeQuery(id+"F45.imprint","IMPRINT",EDGE,{"derivedFrom":sQuery(id+"F45.wireOp",EDGE,"E66.bottom")}),1.0]])]});
            var Q1;
            Q1=makeQuery(id+"F45.imprint","IMPRINT",FACE,{"disambiguationData":[TD([[makeQuery(id+"F45.imprint","IMPRINT",EDGE,{"derivedFrom":sQuery(id+"F45.wireOp",EDGE,"E66.top")}),1.0]])]});
            extrude(context, id + "F46", {"entities" : qUnion([Q0, Q1]), "operationType" : NewBodyOperationType.ADD, "endBound" : BoundingType.UP_TO_NEXT, "oppositeDirection" : true, "depth" : 25 * mm});
        }
        {
            var Q0;
            Q0=makeQuery(id+"F45.imprint","IMPRINT",FACE,{"disambiguationData":[TD([[makeQuery(id+"F45.imprint","IMPRINT",EDGE,{"derivedFrom":sQuery(id+"F45.wireOp",EDGE,"E72.bottom")}),1.0]])]});
            var Q1;
            Q1=makeQuery(id+"F45.imprint","IMPRINT",FACE,{"disambiguationData":[TD([[makeQuery(id+"F45.imprint","IMPRINT",EDGE,{"derivedFrom":sQuery(id+"F45.wireOp",EDGE,"E72.top")}),1.0]])]});
            extrude(context, id + "F47", {"entities" : qUnion([Q0, Q1]), "operationType" : NewBodyOperationType.ADD, "endBound" : BoundingType.UP_TO_NEXT, "oppositeDirection" : true, "depth" : 25 * mm});
        }
        {
            var Q0;
            Q0=makeQuery(id+"F46.opExtrude","SWEPT_FACE",FACE,{"disambiguationData":[OSD([sQuery(id+"F45.wireOp",EDGE,"E66.bottom")])]});
            extrude(context, id + "F48", {"entities" : qUnion([Q0]), "operationType" : NewBodyOperationType.ADD, "endBound" : BoundingType.UP_TO_NEXT, "depth" : 25 * mm});
        }
        {
            var Q0;
            Q0=makeQuery(id+"F47.opExtrude","SWEPT_FACE",FACE,{"disambiguationData":[OSD([sQuery(id+"F45.wireOp",EDGE,"E72.bottom")])]});
            extrude(context, id + "F49", {"entities" : qUnion([Q0]), "operationType" : NewBodyOperationType.ADD, "endBound" : BoundingType.UP_TO_NEXT, "depth" : 25 * mm});
        }
        {
            var Q0;
            Q0=qCreatedBy(makeId("Top.planeOp"),FACE);
            cPlane(context, id + "F50", {"entities" : qUnion([Q0]), "cplaneType" : CPlaneType.OFFSET, "offset" : 40 * mm, "width" : 150 * mm, "height" : 150 * mm});
        }
        {
            var Q0;
            Q0=qCreatedBy(id+"F50.planeOp",FACE);
            var sketch = newSketch(context, id + "F51", { "sketchPlane" : qUnion([Q0])});
            skLineSegment(sketch, "E76.bottom", {"start": v(-5.3, -12.9) * mm, "end": v(0, -12.9) * mm});
            skLineSegment(sketch, "E76.top", {"start": v(-5.3, -3.9) * mm, "end": v(0, -3.9) * mm});
            skLineSegment(sketch, "E76.left", {"start": v(-5.3, -12.9) * mm, "end": v(-5.3, -3.9) * mm});
            skLineSegment(sketch, "E76.right", {"start": v(0, -12.9) * mm, "end": v(0, -3.9) * mm});
            skSolve(sketch);
        }
        {
            var Q0;
            Q0=makeQuery(id+"F51.imprint","IMPRINT",FACE,{"disambiguationData":[TD([[makeQuery(id+"F51.imprint","IMPRINT",EDGE,{"derivedFrom":sQuery(id+"F51.wireOp",EDGE,"E76.bottom")}),1.0]])]});
            extrude(context, id + "F52", {"entities" : qUnion([Q0]), "operationType" : NewBodyOperationType.ADD, "endBound" : BoundingType.UP_TO_NEXT, "oppositeDirection" : true, "depth" : 25 * mm});
        }
        {
            var Q0;
            Q0=makeQuery(id+"F29.imprint","IMPRINT",FACE,{"disambiguationData":[TD([[makeQuery(id+"F29.imprint","IMPRINT",EDGE,{"derivedFrom":sQuery(id+"F29.wireOp",EDGE,"E37.bottom")}),1.0]])]});
            extrude(context, id + "F53", {"entities" : qUnion([Q0]), "operationType" : NewBodyOperationType.REMOVE, "oppositeDirection" : true, "depth" : 1 * mm});
        }
        {
            var Q0;
            {var subQ0=sQuery(id+"F45.wireOp",EDGE,"E66.bottom");Q0=makeQuery(id+"F48.boolean.opBoolean","MERGE",FACE,{"derivedFrom":[makeQuery(id+"F46.opExtrude","CAP_FACE",FACE,{"disambiguationData":[OSD([subQ0,sQuery(id+"F45.wireOp",EDGE,"E66.left"),sQuery(id+"F45.wireOp",EDGE,"E66.right"),sQuery(id+"F45.wireOp",EDGE,"E67"),sQuery(id+"F45.wireOp",EDGE,"E68")])],"isStart":true}),makeQuery(id+"F48.opExtrude","SWEPT_FACE",FACE,{"disambiguationData":[OSD([subQ0])]})]});}
            var sketch = newSketch(context, id + "F54", { "sketchPlane" : qUnion([Q0])});
            skLineSegment(sketch, "E77.bottom", {"start": v(2.73, 25.81) * mm, "end": v(7, 25.81) * mm});
            skLineSegment(sketch, "E77.top", {"start": v(2.73, 22.5) * mm, "end": v(7, 22.5) * mm});
            skLineSegment(sketch, "E77.left", {"start": v(2.73, 25.81) * mm, "end": v(2.73, 22.5) * mm});
            skLineSegment(sketch, "E77.right", {"start": v(7, 25.81) * mm, "end": v(7, 22.5) * mm});
            skLineSegment(sketch, "E78.0", {"start": v(8, 16.5) * mm, "end": v(8, 26.81) * mm});
            skLineSegment(sketch, "E79.0", {"start": v(1.73, 16.5) * mm, "end": v(1.73, 26.81) * mm});
            skPoint(sketch, "E80", {"position": v(4.87, 25.81) * mm});
            skLineSegment(sketch, "E81.bottom", {"start": v(-21, 25.81) * mm, "end": v(-16.7, 25.81) * mm});
            skLineSegment(sketch, "E81.top", {"start": v(-21, 22.5) * mm, "end": v(-16.7, 22.5) * mm});
            skLineSegment(sketch, "E81.left", {"start": v(-21, 25.81) * mm, "end": v(-21, 22.5) * mm});
            skLineSegment(sketch, "E81.right", {"start": v(-16.7, 25.81) * mm, "end": v(-16.7, 22.5) * mm});
            skPoint(sketch, "E82", {"position": v(-18.85, 25.81) * mm});
            skPoint(sketch, "E83", {"position": v(-18.85, 30.4) * mm});
            skSolve(sketch);
        }
        {
            var Q0;
            Q0=makeQuery(id+"F54.imprint","IMPRINT",FACE,{"disambiguationData":[TD([[makeQuery(id+"F54.imprint","IMPRINT",EDGE,{"derivedFrom":sQuery(id+"F54.wireOp",EDGE,"E77.bottom")}),-1.0]])]});
            var Q1;
            Q1=makeQuery(id+"F54.imprint","IMPRINT",FACE,{"disambiguationData":[TD([[makeQuery(id+"F54.imprint","IMPRINT",EDGE,{"derivedFrom":sQuery(id+"F54.wireOp",EDGE,"E81.bottom")}),-1.0]])]});
            extrude(context, id + "F55", {"entities" : qUnion([Q0, Q1]), "operationType" : NewBodyOperationType.REMOVE, "oppositeDirection" : true, "depth" : 1 * mm});
        }
        {
            var Q0;
            Q0=makeQuery(id+"F1.opExtrude","SWEPT_FACE",FACE,{"disambiguationData":[OSD([sQuery(id+"F0.wireOp",EDGE,"E0.top")])]});
            var sketch = newSketch(context, id + "F56", { "sketchPlane" : qUnion([Q0])});
            skLineSegment(sketch, "E84.bottom", {"start": v(-52.53, 0) * mm, "end": v(-34.35, 0) * mm});
            skLineSegment(sketch, "E84.top", {"start": v(-52.53, 10.52) * mm, "end": v(-34.35, 10.52) * mm});
            skLineSegment(sketch, "E84.left", {"start": v(-52.53, 0) * mm, "end": v(-52.53, 10.52) * mm});
            skLineSegment(sketch, "E84.right", {"start": v(-34.35, 0) * mm, "end": v(-34.35, 10.52) * mm});
            skLineSegment(sketch, "E85.bottom", {"start": v(-30.71, 0.5) * mm, "end": v(-26.98, 0.5) * mm});
            skLineSegment(sketch, "E85.top", {"start": v(-30.71, 7.83) * mm, "end": v(-26.98, 7.83) * mm});
            skLineSegment(sketch, "E85.left", {"start": v(-30.71, 0.5) * mm, "end": v(-30.71, 7.83) * mm});
            skLineSegment(sketch, "E85.right", {"start": v(-26.98, 0.5) * mm, "end": v(-26.98, 7.83) * mm});
            skLineSegment(sketch, "E86.bottom", {"start": v(-24.99, 4.88) * mm, "end": v(-18.44, 4.88) * mm});
            skLineSegment(sketch, "E86.top", {"start": v(-24.99, 9.22) * mm, "end": v(-18.44, 9.22) * mm});
            skLineSegment(sketch, "E86.left", {"start": v(-24.99, 4.88) * mm, "end": v(-24.99, 9.22) * mm});
            skLineSegment(sketch, "E86.right", {"start": v(-18.44, 4.88) * mm, "end": v(-18.44, 9.22) * mm});
            skLineSegment(sketch, "E87.bottom", {"start": v(1.92, 6.9) * mm, "end": v(14.01, 6.9) * mm});
            skLineSegment(sketch, "E87.top", {"start": v(1.92, 10.44) * mm, "end": v(14.01, 10.44) * mm});
            skLineSegment(sketch, "E87.left", {"start": v(1.92, 6.9) * mm, "end": v(1.92, 10.44) * mm});
            skLineSegment(sketch, "E87.right", {"start": v(14.01, 6.9) * mm, "end": v(14.01, 10.44) * mm});
            skLineSegment(sketch, "E88.bottom", {"start": v(-12.34, 3.5) * mm, "end": v(-9.64, 3.5) * mm});
            skLineSegment(sketch, "E88.top", {"start": v(-12.34, 9.47) * mm, "end": v(-9.64, 9.47) * mm});
            skLineSegment(sketch, "E88.left", {"start": v(-12.34, 3.5) * mm, "end": v(-12.34, 9.47) * mm});
            skLineSegment(sketch, "E88.right", {"start": v(-9.64, 3.5) * mm, "end": v(-9.64, 9.47) * mm});
            skLineSegment(sketch, "E89.bottom", {"start": v(-9.04, 3.5) * mm, "end": v(-6.34, 3.5) * mm});
            skLineSegment(sketch, "E89.top", {"start": v(-9.04, 9.47) * mm, "end": v(-6.34, 9.47) * mm});
            skLineSegment(sketch, "E89.left", {"start": v(-9.04, 3.5) * mm, "end": v(-9.04, 9.47) * mm});
            skLineSegment(sketch, "E89.right", {"start": v(-6.34, 3.5) * mm, "end": v(-6.34, 9.47) * mm});
            skSolve(sketch);
        }
        {
            var Q0;
            Q0=makeQuery(id+"F56.imprint","IMPRINT",FACE,{"disambiguationData":[TD([[makeQuery(id+"F56.imprint","IMPRINT",EDGE,{"derivedFrom":sQuery(id+"F56.wireOp",EDGE,"E84.bottom")}),1.0]])]});
            var Q1;
            Q1=makeQuery(id+"F56.imprint","IMPRINT",FACE,{"disambiguationData":[TD([[makeQuery(id+"F56.imprint","IMPRINT",EDGE,{"derivedFrom":sQuery(id+"F56.wireOp",EDGE,"E85.bottom")}),1.0]])]});
            var Q2;
            Q2=makeQuery(id+"F56.imprint","IMPRINT",FACE,{"disambiguationData":[TD([[makeQuery(id+"F56.imprint","IMPRINT",EDGE,{"derivedFrom":sQuery(id+"F56.wireOp",EDGE,"E86.bottom")}),1.0]])]});
            var Q3;
            Q3=makeQuery(id+"F56.imprint","IMPRINT",FACE,{"disambiguationData":[TD([[makeQuery(id+"F56.imprint","IMPRINT",EDGE,{"derivedFrom":sQuery(id+"F56.wireOp",EDGE,"E88.bottom")}),1.0]])]});
            var Q4;
            Q4=makeQuery(id+"F56.imprint","IMPRINT",FACE,{"disambiguationData":[TD([[makeQuery(id+"F56.imprint","IMPRINT",EDGE,{"derivedFrom":sQuery(id+"F56.wireOp",EDGE,"E89.bottom")}),1.0]])]});
            var Q5;
            Q5=makeQuery(id+"F56.imprint","IMPRINT",FACE,{"disambiguationData":[TD([[makeQuery(id+"F56.imprint","IMPRINT",EDGE,{"derivedFrom":sQuery(id+"F56.wireOp",EDGE,"E87.bottom")}),1.0]])]});
            extrude(context, id + "F57", {"entities" : qUnion([Q0, Q1, Q2, Q3, Q4, Q5]), "operationType" : NewBodyOperationType.REMOVE, "oppositeDirection" : true, "depth" : 1 * mm});
        }
        {
            var Q0;
            Q0=qCreatedBy(makeId("Top.planeOp"),FACE);
            var sketch = newSketch(context, id + "F58", { "sketchPlane" : qUnion([Q0])});
            skLineSegment(sketch, "E90.0", {"start": v(-54, 17.76) * mm, "end": v(24, 17.76) * mm});
            skCircle(sketch, "E91.cCircle", {"center": v(-15, 17.76) * mm, "radius": 4.76 * mm, "construction": true});
            skLineSegment(sketch, "E91.0", {"start": v(-16.54, 22.52) * mm, "end": v(-13.45, 22.52) * mm});
            skLineSegment(sketch, "E91.1", {"start": v(-13.45, 22.52) * mm, "end": v(-10.95, 20.7) * mm});
            skLineSegment(sketch, "E91.2", {"start": v(-10.95, 20.7) * mm, "end": v(-10, 17.76) * mm});
            skLineSegment(sketch, "E91.3", {"start": v(-10, 17.76) * mm, "end": v(-10.95, 14.83) * mm});
            skLineSegment(sketch, "E91.4", {"start": v(-10.95, 14.83) * mm, "end": v(-13.45, 13) * mm});
            skLineSegment(sketch, "E91.5", {"start": v(-13.45, 13) * mm, "end": v(-16.54, 13) * mm});
            skLineSegment(sketch, "E91.6", {"start": v(-16.54, 13) * mm, "end": v(-19.04, 14.83) * mm});
            skLineSegment(sketch, "E91.7", {"start": v(-19.04, 14.83) * mm, "end": v(-20, 17.76) * mm});
            skLineSegment(sketch, "E91.8", {"start": v(-20, 17.76) * mm, "end": v(-19.04, 20.7) * mm});
            skLineSegment(sketch, "E91.9", {"start": v(-19.04, 20.7) * mm, "end": v(-16.54, 22.52) * mm});
            skPoint(sketch, "E91.0.midPoint", {"position": v(-15, 22.52) * mm});
            skLineSegment(sketch, "E92.0", {"start": v(-13.77, 21.52) * mm, "end": v(-11.8, 20.08) * mm});
            skLineSegment(sketch, "E92.1", {"start": v(-16.21, 21.52) * mm, "end": v(-13.77, 21.52) * mm});
            skLineSegment(sketch, "E92.2", {"start": v(-11.8, 20.08) * mm, "end": v(-11.04, 17.76) * mm});
            skLineSegment(sketch, "E92.3", {"start": v(-18.19, 20.08) * mm, "end": v(-16.21, 21.52) * mm});
            skLineSegment(sketch, "E92.4", {"start": v(-18.94, 17.76) * mm, "end": v(-18.19, 20.08) * mm});
            skLineSegment(sketch, "E92.5", {"start": v(-18.19, 15.44) * mm, "end": v(-18.94, 17.76) * mm});
            skLineSegment(sketch, "E92.6", {"start": v(-11.04, 17.76) * mm, "end": v(-11.8, 15.44) * mm});
            skLineSegment(sketch, "E92.7", {"start": v(-11.8, 15.44) * mm, "end": v(-13.77, 14) * mm});
            skLineSegment(sketch, "E92.8", {"start": v(-13.77, 14) * mm, "end": v(-16.21, 14) * mm});
            skLineSegment(sketch, "E92.9", {"start": v(-16.21, 14) * mm, "end": v(-18.19, 15.44) * mm});
            skLineSegment(sketch, "E93", {"start": v(-11.8, 20.08) * mm, "end": v(-10.85, 20.4) * mm});
            skLineSegment(sketch, "E94", {"start": v(-11.8, 20.08) * mm, "end": v(-11.2, 20.9) * mm});
            skLineSegment(sketch, "E95", {"start": v(-13.77, 21.52) * mm, "end": v(-13.18, 22.33) * mm});
            skLineSegment(sketch, "E96", {"start": v(-13.77, 21.52) * mm, "end": v(-13.77, 22.52) * mm});
            skLineSegment(sketch, "E97", {"start": v(-16.21, 21.52) * mm, "end": v(-16.21, 22.52) * mm});
            skLineSegment(sketch, "E98", {"start": v(-16.21, 21.52) * mm, "end": v(-16.8, 22.33) * mm});
            skLineSegment(sketch, "E99", {"start": v(-18.19, 20.08) * mm, "end": v(-18.77, 20.9) * mm});
            skLineSegment(sketch, "E100", {"start": v(-18.19, 20.08) * mm, "end": v(-19.14, 20.4) * mm});
            skLineSegment(sketch, "E101", {"start": v(-18.94, 17.76) * mm, "end": v(-19.9, 18.07) * mm});
            skLineSegment(sketch, "E102", {"start": v(-11.04, 17.76) * mm, "end": v(-10.1, 18.07) * mm});
            skSolve(sketch);
        }
        {
            var Q0;
            Q0=makeQuery(id+"F58.imprint","IMPRINT",FACE,{"disambiguationData":[TD([[makeQuery(id+"F58.imprint","IMPRINT",EDGE,{"derivedFrom":sQuery(id+"F58.wireOp",EDGE,"E92.1")}),1.0]])]});
            var Q1;
            {var subQ4=sQuery(id+"F58.wireOp",EDGE,"E95");Q1=makeQuery(id+"F58.imprint","IMPRINT",FACE,{"disambiguationData":[TD([[makeQuery(id+"F58.imprint","IMPRINT",EDGE,{"derivedFrom":subQ4}),1.0]])]});}
            var Q2;
            {var subQ3=sQuery(id+"F58.wireOp",EDGE,"E97");Q2=makeQuery(id+"F58.imprint","IMPRINT",FACE,{"disambiguationData":[TD([[makeQuery(id+"F58.imprint","IMPRINT",EDGE,{"derivedFrom":subQ3}),1.0]])]});}
            var Q3;
            Q3=makeQuery(id+"F58.imprint","IMPRINT",FACE,{"disambiguationData":[TD([[makeQuery(id+"F58.imprint","IMPRINT",EDGE,{"derivedFrom":sQuery(id+"F58.wireOp",EDGE,"E92.3")}),1.0]])]});
            var Q4;
            {var subQ4=sQuery(id+"F58.wireOp",EDGE,"E99");Q4=makeQuery(id+"F58.imprint","IMPRINT",FACE,{"disambiguationData":[TD([[makeQuery(id+"F58.imprint","IMPRINT",EDGE,{"derivedFrom":subQ4}),1.0]])]});}
            var Q5;
            Q5=makeQuery(id+"F58.imprint","IMPRINT",FACE,{"disambiguationData":[TD([[makeQuery(id+"F58.imprint","IMPRINT",EDGE,{"derivedFrom":sQuery(id+"F58.wireOp",EDGE,"E92.4")}),1.0]])]});
            var Q6;
            {var subQ3=sQuery(id+"F58.wireOp",EDGE,"E101");Q6=makeQuery(id+"F58.imprint","IMPRINT",FACE,{"disambiguationData":[TD([[makeQuery(id+"F58.imprint","IMPRINT",EDGE,{"derivedFrom":subQ3}),1.0]])]});}
            var Q7;
            {var subQ4=sQuery(id+"F58.wireOp",EDGE,"E93");Q7=makeQuery(id+"F58.imprint","IMPRINT",FACE,{"disambiguationData":[TD([[makeQuery(id+"F58.imprint","IMPRINT",EDGE,{"derivedFrom":subQ4}),1.0]])]});}
            var Q8;
            Q8=makeQuery(id+"F58.imprint","IMPRINT",FACE,{"disambiguationData":[TD([[makeQuery(id+"F58.imprint","IMPRINT",EDGE,{"derivedFrom":sQuery(id+"F58.wireOp",EDGE,"E92.2")}),1.0]])]});
            var Q9;
            {var subQ3=sQuery(id+"F58.wireOp",EDGE,"E102");Q9=makeQuery(id+"F58.imprint","IMPRINT",FACE,{"disambiguationData":[TD([[makeQuery(id+"F58.imprint","IMPRINT",EDGE,{"derivedFrom":subQ3}),-1.0]])]});}
            var Q10;
            Q10=makeQuery(id+"F58.imprint","IMPRINT",FACE,{"disambiguationData":[TD([[makeQuery(id+"F58.imprint","IMPRINT",EDGE,{"derivedFrom":sQuery(id+"F58.wireOp",EDGE,"E92.0")}),1.0]])]});
            var Q11;
            Q11=makeQuery(id+"F58.imprint","IMPRINT",FACE,{"disambiguationData":[TD([[makeQuery(id+"F58.imprint","IMPRINT",EDGE,{"derivedFrom":sQuery(id+"F58.wireOp",EDGE,"E92.0")}),-1.0]])]});
            extrude(context, id + "F59", {"entities" : qUnion([Q0, Q1, Q2, Q3, Q4, Q5, Q6, Q7, Q8, Q9, Q10, Q11]), "operationType" : NewBodyOperationType.ADD, "depth" : 12 * mm});
        }
        {
            var Q0;
            Q0=qCreatedBy(makeId("Right.planeOp"),FACE);
            cPlane(context, id + "F60", {"entities" : qUnion([Q0]), "cplaneType" : CPlaneType.OFFSET, "offset" : 8.7 * mm, "oppositeDirection" : true, "width" : 150 * mm, "height" : 150 * mm});
        }
        {
            var Q0;
            Q0=qCreatedBy(id+"F60.planeOp",FACE);
            var sketch = newSketch(context, id + "F61", { "sketchPlane" : qUnion([Q0])});
            skLineSegment(sketch, "E103.0", {"start": v(0, 33.97) * mm, "end": v(17.76, 12) * mm});
            skPoint(sketch, "E104.0", {"position": v(22.52, 12) * mm});
            skLineSegment(sketch, "E105.0", {"start": v(20.7, 12) * mm, "end": v(17.76, 12) * mm});
            skLineSegment(sketch, "E106.0", {"start": v(22.52, 12) * mm, "end": v(20.7, 12) * mm});
            skLineSegment(sketch, "E107", {"start": v(14.45, 16.1) * mm, "end": v(23.69, 12) * mm});
            skLineSegment(sketch, "E108", {"start": v(23.69, 12) * mm, "end": v(22.52, 12) * mm});
            skSolve(sketch);
        }
        {
            var Q0;
            {var subQ1=sQuery(id+"F61.wireOp",EDGE,"E105.0");Q0=makeQuery(id+"F61.imprint","IMPRINT",FACE,{"disambiguationData":[TD([[makeQuery(id+"F61.imprint","IMPRINT",EDGE,{"derivedFrom":subQ1}),-1.0]])]});}
            extrude(context, id + "F62", {"entities" : qUnion([Q0]), "operationType" : NewBodyOperationType.ADD, "oppositeDirection" : true, "depth" : 12.1 * mm});
        }
        {
            var Q0;
            Q0=makeQuery(id+"F59.opExtrude","SWEPT_FACE",FACE,{"disambiguationData":[OSD([sQuery(id+"F58.wireOp",EDGE,"E91.0")])]});
            var sketch = newSketch(context, id + "F63", { "sketchPlane" : qUnion([Q0])});
            skLineSegment(sketch, "E109.bottom", {"start": v(13.8, 4) * mm, "end": v(16.19, 4) * mm});
            skLineSegment(sketch, "E109.top", {"start": v(13.8, 10.5) * mm, "end": v(16.19, 10.5) * mm});
            skLineSegment(sketch, "E109.left", {"start": v(13.8, 4) * mm, "end": v(13.8, 10.5) * mm});
            skLineSegment(sketch, "E109.right", {"start": v(16.19, 4) * mm, "end": v(16.19, 10.5) * mm});
            skLineSegment(sketch, "E110", {"start": v(13.45, 7.68) * mm, "end": v(13.8, 7.68) * mm, "construction": true});
            skLineSegment(sketch, "E111", {"start": v(16.19, 7.82) * mm, "end": v(16.54, 7.82) * mm, "construction": true});
            skLineSegment(sketch, "E112.0", {"start": v(16.54, 12) * mm, "end": v(13.45, 12) * mm});
            skLineSegment(sketch, "E113.0", {"start": v(16.54, 0) * mm, "end": v(13.45, 0) * mm});
            skSolve(sketch);
        }
        {
            var Q0;
            Q0=makeQuery(id+"F59.opExtrude","SWEPT_FACE",FACE,{"disambiguationData":[OSD([sQuery(id+"F58.wireOp",EDGE,"E91.9")])]});
            var sketch = newSketch(context, id + "F64", { "sketchPlane" : qUnion([Q0])});
            skLineSegment(sketch, "E114.bottom", {"start": v(0.5, 4) * mm, "end": v(2.88, 4) * mm});
            skLineSegment(sketch, "E114.top", {"start": v(0.5, 10.5) * mm, "end": v(2.88, 10.5) * mm});
            skLineSegment(sketch, "E114.left", {"start": v(0.5, 4) * mm, "end": v(0.5, 10.5) * mm});
            skLineSegment(sketch, "E114.right", {"start": v(2.88, 4) * mm, "end": v(2.88, 10.5) * mm});
            skLineSegment(sketch, "E115", {"start": v(0.5, 8) * mm, "end": v(0.14, 8) * mm, "construction": true});
            skLineSegment(sketch, "E116", {"start": v(2.88, 7.25) * mm, "end": v(3.23, 7.25) * mm, "construction": true});
            skLineSegment(sketch, "E117.0", {"start": v(3.23, 12) * mm, "end": v(0.14, 12) * mm});
            skLineSegment(sketch, "E118.0", {"start": v(3.23, 0) * mm, "end": v(0.14, 0) * mm});
            skSolve(sketch);
        }
        {
            var Q0;
            Q0=makeQuery(id+"F63.imprint","IMPRINT",FACE,{"disambiguationData":[TD([[makeQuery(id+"F63.imprint","IMPRINT",EDGE,{"derivedFrom":sQuery(id+"F63.wireOp",EDGE,"E109.bottom")}),1.0]])]});
            extrude(context, id + "F65", {"entities" : qUnion([Q0]), "operationType" : NewBodyOperationType.REMOVE, "oppositeDirection" : true, "depth" : 1 * mm});
        }
        {
            var Q0;
            Q0=makeQuery(id+"F64.imprint","IMPRINT",FACE,{"disambiguationData":[TD([[makeQuery(id+"F64.imprint","IMPRINT",EDGE,{"derivedFrom":sQuery(id+"F64.wireOp",EDGE,"E114.bottom")}),1.0]])]});
            extrude(context, id + "F66", {"entities" : qUnion([Q0]), "operationType" : NewBodyOperationType.REMOVE, "oppositeDirection" : true, "depth" : 1 * mm});
        }
        {
            var Q0;
            Q0=makeQuery(id+"F59.opExtrude","SWEPT_FACE",FACE,{"disambiguationData":[OSD([sQuery(id+"F58.wireOp",EDGE,"E91.8")])]});
            var sketch = newSketch(context, id + "F67", { "sketchPlane" : qUnion([Q0])});
            skLineSegment(sketch, "E119.0", {"start": v(-10.72, 12) * mm, "end": v(-13.8, 12) * mm});
            skLineSegment(sketch, "E120.0", {"start": v(-10.72, 0) * mm, "end": v(-13.8, 0) * mm});
            skLineSegment(sketch, "E121.bottom", {"start": v(-13.46, 4) * mm, "end": v(-11.07, 4) * mm});
            skLineSegment(sketch, "E121.top", {"start": v(-13.46, 10.5) * mm, "end": v(-11.07, 10.5) * mm});
            skLineSegment(sketch, "E121.left", {"start": v(-13.46, 4) * mm, "end": v(-13.46, 10.5) * mm});
            skLineSegment(sketch, "E121.right", {"start": v(-11.07, 4) * mm, "end": v(-11.07, 10.5) * mm});
            skLineSegment(sketch, "E122", {"start": v(-13.46, 7.63) * mm, "end": v(-13.8, 7.63) * mm, "construction": true});
            skLineSegment(sketch, "E123", {"start": v(-11.07, 7.82) * mm, "end": v(-10.72, 7.82) * mm, "construction": true});
            skLineSegment(sketch, "E124.0", {"start": v(-13.8, 12) * mm, "end": v(-13.8, 0) * mm});
            skSolve(sketch);
        }
        {
            var Q0;
            Q0=makeQuery(id+"F66.boolean.opBoolean","COPY",EDGE,{"derivedFrom":makeQuery(id+"F66.opExtrude","CAP_EDGE",EDGE,{"disambiguationData":[OSD([sQuery(id+"F64.wireOp",EDGE,"E114.left")])],"isStart":false})});
            var Q1;
            Q1=makeQuery(id+"F65.boolean.opBoolean","COPY",EDGE,{"derivedFrom":makeQuery(id+"F65.opExtrude","CAP_EDGE",EDGE,{"disambiguationData":[OSD([sQuery(id+"F63.wireOp",EDGE,"E109.right")])],"isStart":false})});
            chamfer(context, id + "F68", {"entities" : qUnion([Q0, Q1]), "width" : .5 * mm, "tangentPropagation" : true});
        }
        {
            var Q0;
            Q0=makeQuery(id+"F67.imprint","IMPRINT",FACE,{"disambiguationData":[TD([[makeQuery(id+"F67.imprint","IMPRINT",EDGE,{"derivedFrom":sQuery(id+"F67.wireOp",EDGE,"E121.bottom")}),1.0]])]});
            extrude(context, id + "F69", {"entities" : qUnion([Q0]), "operationType" : NewBodyOperationType.REMOVE, "oppositeDirection" : true, "depth" : 1 * mm});
        }
        {
            var Q0;
            Q0=makeQuery(id+"F66.boolean.opBoolean","COPY",EDGE,{"derivedFrom":makeQuery(id+"F66.opExtrude","CAP_EDGE",EDGE,{"disambiguationData":[OSD([sQuery(id+"F64.wireOp",EDGE,"E114.right")])],"isStart":false})});
            var Q1;
            Q1=makeQuery(id+"F69.boolean.opBoolean","COPY",EDGE,{"derivedFrom":makeQuery(id+"F69.opExtrude","CAP_EDGE",EDGE,{"disambiguationData":[OSD([sQuery(id+"F67.wireOp",EDGE,"E121.left")])],"isStart":false})});
            chamfer(context, id + "F70", {"entities" : qUnion([Q0, Q1]), "width" : .5 * mm, "tangentPropagation" : true});
        }
        {
            var Q0;
            Q0=makeQuery(id+"F59.opExtrude","SWEPT_FACE",FACE,{"disambiguationData":[OSD([sQuery(id+"F58.wireOp",EDGE,"E91.1")])]});
            var sketch = newSketch(context, id + "F71", { "sketchPlane" : qUnion([Q0])});
            skLineSegment(sketch, "E125.bottom", {"start": v(23.77, 4) * mm, "end": v(21.37, 4) * mm});
            skLineSegment(sketch, "E125.top", {"start": v(23.77, 10.5) * mm, "end": v(21.37, 10.5) * mm});
            skLineSegment(sketch, "E125.left", {"start": v(23.77, 4) * mm, "end": v(23.77, 10.5) * mm});
            skLineSegment(sketch, "E125.right", {"start": v(21.37, 4) * mm, "end": v(21.37, 10.5) * mm});
            skLineSegment(sketch, "E126.0", {"start": v(24.12, 12) * mm, "end": v(21.02, 12) * mm});
            skLineSegment(sketch, "E127.0", {"start": v(21.02, 12) * mm, "end": v(21.02, 0) * mm});
            skLineSegment(sketch, "E128.0", {"start": v(24.12, 12) * mm, "end": v(24.12, 0) * mm});
            skLineSegment(sketch, "E129", {"start": v(23.77, 6.6) * mm, "end": v(24.12, 6.6) * mm, "construction": true});
            skLineSegment(sketch, "E130", {"start": v(21.37, 7) * mm, "end": v(21.02, 7) * mm, "construction": true});
            skSolve(sketch);
        }
        {
            var Q0;
            Q0=makeQuery(id+"F22.opExtrude","SWEPT_FACE",FACE,{"disambiguationData":[OSD([sQuery(id+"F17.wireOp",EDGE,"E22.right")])]});
            var sketch = newSketch(context, id + "F72", { "sketchPlane" : qUnion([Q0])});
            skLineSegment(sketch, "E131.bottom", {"start": v(27.24, 11.5) * mm, "end": v(28.24, 11.5) * mm});
            skLineSegment(sketch, "E131.top", {"start": v(27.24, 11) * mm, "end": v(28.24, 11) * mm});
            skLineSegment(sketch, "E131.left", {"start": v(28.24, 11.5) * mm, "end": v(28.24, 11) * mm});
            skLineSegment(sketch, "E131.right", {"start": v(27.24, 11.5) * mm, "end": v(27.24, 11) * mm});
            skSolve(sketch);
        }
        {
            var Q0;
            Q0 = qSketchRegion(id + "F72", true);
            var Q1;
            Q1=makeQuery(id+"F23.opExtrude","SWEPT_FACE",FACE,{"disambiguationData":[OSD([sQuery(id+"F13.wireOp",EDGE,"E18.right")])]});
            extrude(context, id + "F73", {"entities" : qUnion([Q0]), "operationType" : NewBodyOperationType.ADD, "endBound" : BoundingType.UP_TO_SURFACE, "endBoundEntityFace" : qUnion([Q1]), "depth" : 25 * mm});
        }
        {
            var Q0;
            Q0=makeQuery(id+"F71.imprint","IMPRINT",FACE,{"disambiguationData":[TD([[makeQuery(id+"F71.imprint","IMPRINT",EDGE,{"derivedFrom":sQuery(id+"F71.wireOp",EDGE,"E125.bottom")}),-1.0]])]});
            extrude(context, id + "F74", {"entities" : qUnion([Q0]), "operationType" : NewBodyOperationType.REMOVE, "oppositeDirection" : true, "depth" : 1 * mm});
        }
        {
            var Q0;
            Q0=makeQuery(id+"F74.boolean.opBoolean","COPY",EDGE,{"derivedFrom":makeQuery(id+"F74.opExtrude","CAP_EDGE",EDGE,{"disambiguationData":[OSD([sQuery(id+"F71.wireOp",EDGE,"E125.left")])],"isStart":false})});
            var Q1;
            Q1=makeQuery(id+"F65.boolean.opBoolean","COPY",EDGE,{"derivedFrom":makeQuery(id+"F65.opExtrude","CAP_EDGE",EDGE,{"disambiguationData":[OSD([sQuery(id+"F63.wireOp",EDGE,"E109.left")])],"isStart":false})});
            chamfer(context, id + "F75", {"entities" : qUnion([Q0, Q1]), "width" : .5 * mm, "tangentPropagation" : true});
        }
        {
            var Q0;
            Q0=makeQuery(id+"F59.opExtrude","SWEPT_FACE",FACE,{"disambiguationData":[OSD([sQuery(id+"F58.wireOp",EDGE,"E91.2")])]});
            var sketch = newSketch(context, id + "F76", { "sketchPlane" : qUnion([Q0])});
            skLineSegment(sketch, "E132.bottom", {"start": v(20.33, 4) * mm, "end": v(22.72, 4) * mm});
            skLineSegment(sketch, "E132.top", {"start": v(20.33, 10.5) * mm, "end": v(22.72, 10.5) * mm});
            skLineSegment(sketch, "E132.left", {"start": v(20.33, 4) * mm, "end": v(20.33, 10.5) * mm});
            skLineSegment(sketch, "E132.right", {"start": v(22.72, 4) * mm, "end": v(22.72, 10.5) * mm});
            skLineSegment(sketch, "E133.0.0", {"start": v(19.98, 0) * mm, "end": v(23.07, 0) * mm});
            skLineSegment(sketch, "E133.0.1", {"start": v(23.07, 0) * mm, "end": v(23.07, 12) * mm});
            skLineSegment(sketch, "E133.0.2", {"start": v(23.07, 12) * mm, "end": v(19.98, 12) * mm});
            skLineSegment(sketch, "E133.0.3", {"start": v(19.98, 12) * mm, "end": v(19.98, 0) * mm});
            skLineSegment(sketch, "E134", {"start": v(23.07, 7.8) * mm, "end": v(22.72, 7.8) * mm, "construction": true});
            skLineSegment(sketch, "E135", {"start": v(20.33, 7.9) * mm, "end": v(19.98, 7.9) * mm, "construction": true});
            skSolve(sketch);
        }
        {
            var Q0;
            Q0=makeQuery(id+"F76.imprint","IMPRINT",FACE,{"disambiguationData":[TD([[makeQuery(id+"F76.imprint","IMPRINT",EDGE,{"derivedFrom":sQuery(id+"F76.wireOp",EDGE,"E132.bottom")}),1.0]])]});
            extrude(context, id + "F77", {"entities" : qUnion([Q0]), "operationType" : NewBodyOperationType.REMOVE, "oppositeDirection" : true, "depth" : 1 * mm});
        }
        {
            var Q0;
            Q0=makeQuery(id+"F77.boolean.opBoolean","COPY",EDGE,{"derivedFrom":makeQuery(id+"F77.opExtrude","CAP_EDGE",EDGE,{"disambiguationData":[OSD([sQuery(id+"F76.wireOp",EDGE,"E132.right")])],"isStart":false})});
            var Q1;
            Q1=makeQuery(id+"F74.boolean.opBoolean","COPY",EDGE,{"derivedFrom":makeQuery(id+"F74.opExtrude","CAP_EDGE",EDGE,{"disambiguationData":[OSD([sQuery(id+"F71.wireOp",EDGE,"E125.right")])],"isStart":false})});
            chamfer(context, id + "F78", {"entities" : qUnion([Q0, Q1]), "width" : .5 * mm, "tangentPropagation" : true});
        }
        {
            var Q0;
            Q0=makeQuery(id+"F29.imprint","IMPRINT",FACE,{"disambiguationData":[TD([[makeQuery(id+"F29.imprint","IMPRINT",EDGE,{"derivedFrom":sQuery(id+"F29.wireOp",EDGE,"E41.bottom")}),1.0]])]});
            var Q1;
            Q1=makeQuery(id+"F29.imprint","IMPRINT",FACE,{"disambiguationData":[TD([[makeQuery(id+"F29.imprint","IMPRINT",EDGE,{"derivedFrom":sQuery(id+"F29.wireOp",EDGE,"E42.bottom")}),1.0]])]});
            var Q2;
            Q2=makeQuery(id+"F29.imprint","IMPRINT",FACE,{"disambiguationData":[TD([[makeQuery(id+"F29.imprint","IMPRINT",EDGE,{"derivedFrom":sQuery(id+"F29.wireOp",EDGE,"E43.bottom")}),1.0]])]});
            var Q3;
            Q3=makeQuery(id+"F29.imprint","IMPRINT",FACE,{"disambiguationData":[TD([[makeQuery(id+"F29.imprint","IMPRINT",EDGE,{"derivedFrom":sQuery(id+"F29.wireOp",EDGE,"E44.bottom")}),-1.0]])]});
            extrude(context, id + "F79", {"entities" : qUnion([Q0, Q1, Q2, Q3]), "operationType" : NewBodyOperationType.REMOVE, "oppositeDirection" : true, "depth" : 1 * mm});
        }
        {
            var Q0;
            Q0=makeQuery(id+"F3.opExtrude","CAP_FACE",FACE,{"disambiguationData":[OSD([sQuery(id+"F2.wireOp",EDGE,"E1.0"),sQuery(id+"F2.wireOp",EDGE,"E2"),sQuery(id+"F2.wireOp",EDGE,"E3")])],"isStart":false});
            var sketch = newSketch(context, id + "F80", { "sketchPlane" : qUnion([Q0])});
            skLineSegment(sketch, "E136.bottom", {"start": v(-3.85, 20.33) * mm, "end": v(3.85, 20.33) * mm});
            skLineSegment(sketch, "E136.top", {"start": v(-3.85, 24.93) * mm, "end": v(3.85, 24.93) * mm});
            skLineSegment(sketch, "E136.left", {"start": v(-3.85, 20.33) * mm, "end": v(-3.85, 24.93) * mm});
            skLineSegment(sketch, "E136.right", {"start": v(3.85, 20.33) * mm, "end": v(3.85, 24.93) * mm});
            skPoint(sketch, "E137", {"position": v(0, 24.93) * mm});
            skSolve(sketch);
        }
        {
            var Q0;
            Q0=makeQuery(id+"F80.imprint","IMPRINT",FACE,{"disambiguationData":[TD([[makeQuery(id+"F80.imprint","IMPRINT",EDGE,{"derivedFrom":sQuery(id+"F80.wireOp",EDGE,"E136.bottom")}),1.0]])]});
            extrude(context, id + "F81", {"entities" : qUnion([Q0]), "operationType" : NewBodyOperationType.REMOVE, "oppositeDirection" : true, "depth" : 1 * mm});
        }
        {
            var Q0;
            {var subQ13=sQuery(id+"F0.wireOp",EDGE,"E0.right");var subQ14=sQuery(id+"F0.wireOp",EDGE,"E0.bottom");Q0=makeQuery(id+"F59.boolean.opBoolean","SPLIT",FACE,{"disambiguationData":[TD([makeQuery(id+"F1.opExtrude","SWEPT_FACE",FACE,{"disambiguationData":[OSD([subQ13])]})])],"derivedFrom":makeQuery(id+"F30.boolean.opBoolean","MERGE",FACE,{"derivedFrom":[makeQuery(id+"F1.opExtrude","SWEPT_FACE",FACE,{"disambiguationData":[OSD([subQ14])]}),makeQuery(id+"F30.opExtrude","SWEPT_FACE",FACE,{"disambiguationData":[OSD([subQ14,subQ13])]})]})});}
            var sketch = newSketch(context, id + "F82", { "sketchPlane" : qUnion([Q0])});
            skPoint(sketch, "E138.0", {"position": v(-18, 6.72) * mm});
            skLineSegment(sketch, "E139.bottom", {"start": v(-14.34, 5.2) * mm, "end": v(-5.78, 5.2) * mm});
            skLineSegment(sketch, "E139.top", {"start": v(-14.34, 10.71) * mm, "end": v(-5.78, 10.71) * mm});
            skLineSegment(sketch, "E139.left", {"start": v(-14.34, 5.2) * mm, "end": v(-14.34, 10.71) * mm});
            skLineSegment(sketch, "E139.right", {"start": v(-5.78, 5.2) * mm, "end": v(-5.78, 10.71) * mm});
            skLineSegment(sketch, "E140.bottom", {"start": v(3.2, 7.43) * mm, "end": v(5.48, 7.43) * mm});
            skLineSegment(sketch, "E140.top", {"start": v(3.2, 10.7) * mm, "end": v(5.48, 10.7) * mm});
            skLineSegment(sketch, "E140.left", {"start": v(3.2, 7.43) * mm, "end": v(3.2, 10.7) * mm});
            skLineSegment(sketch, "E140.right", {"start": v(5.48, 7.43) * mm, "end": v(5.48, 10.7) * mm});
            skSolve(sketch);
        }
        {
            var Q0;
            Q0=makeQuery(id+"F82.imprint","IMPRINT",FACE,{"disambiguationData":[TD([[makeQuery(id+"F82.imprint","IMPRINT",EDGE,{"derivedFrom":sQuery(id+"F82.wireOp",EDGE,"E139.bottom")}),1.0]])]});
            extrude(context, id + "F83", {"entities" : qUnion([Q0]), "operationType" : NewBodyOperationType.REMOVE, "oppositeDirection" : true, "depth" : 1 * mm});
        }
        {
            var Q0;
            Q0=makeQuery(id+"F82.imprint","IMPRINT",FACE,{"disambiguationData":[TD([[makeQuery(id+"F82.imprint","IMPRINT",EDGE,{"derivedFrom":sQuery(id+"F82.wireOp",EDGE,"E140.bottom")}),1.0]])]});
            extrude(context, id + "F84", {"entities" : qUnion([Q0]), "operationType" : NewBodyOperationType.REMOVE, "oppositeDirection" : true, "depth" : 1 * mm});
        }
        {
            var Q0;
            Q0=makeQuery(id+"F39.opExtrude","SWEPT_FACE",FACE,{"disambiguationData":[OSD([sQuery(id+"F38.wireOp",EDGE,"E56.top")])]});
            var sketch = newSketch(context, id + "F85", { "sketchPlane" : qUnion([Q0])});
            skLineSegment(sketch, "E141.bottom", {"start": v(-24, 11.5) * mm, "end": v(-23, 11.5) * mm});
            skLineSegment(sketch, "E141.top", {"start": v(-24, 12) * mm, "end": v(-23, 12) * mm});
            skLineSegment(sketch, "E141.left", {"start": v(-24, 11.5) * mm, "end": v(-24, 12) * mm});
            skLineSegment(sketch, "E141.right", {"start": v(-23, 11.5) * mm, "end": v(-23, 12) * mm});
            skSolve(sketch);
        }
        {
            var Q0;
            Q0=makeQuery(id+"F85.imprint","IMPRINT",FACE,{"disambiguationData":[TD([[makeQuery(id+"F85.imprint","IMPRINT",EDGE,{"derivedFrom":sQuery(id+"F85.wireOp",EDGE,"E141.bottom")}),1.0]])]});
            var Q1;
            Q1=makeQuery(id+"F43.opExtrude","SWEPT_FACE",FACE,{"disambiguationData":[OSD([sQuery(id+"F38.wireOp",EDGE,"E61.top")])]});
            extrude(context, id + "F86", {"entities" : qUnion([Q0]), "operationType" : NewBodyOperationType.ADD, "endBound" : BoundingType.UP_TO_SURFACE, "endBoundEntityFace" : qUnion([Q1]), "depth" : 25 * mm});
        }
    });
